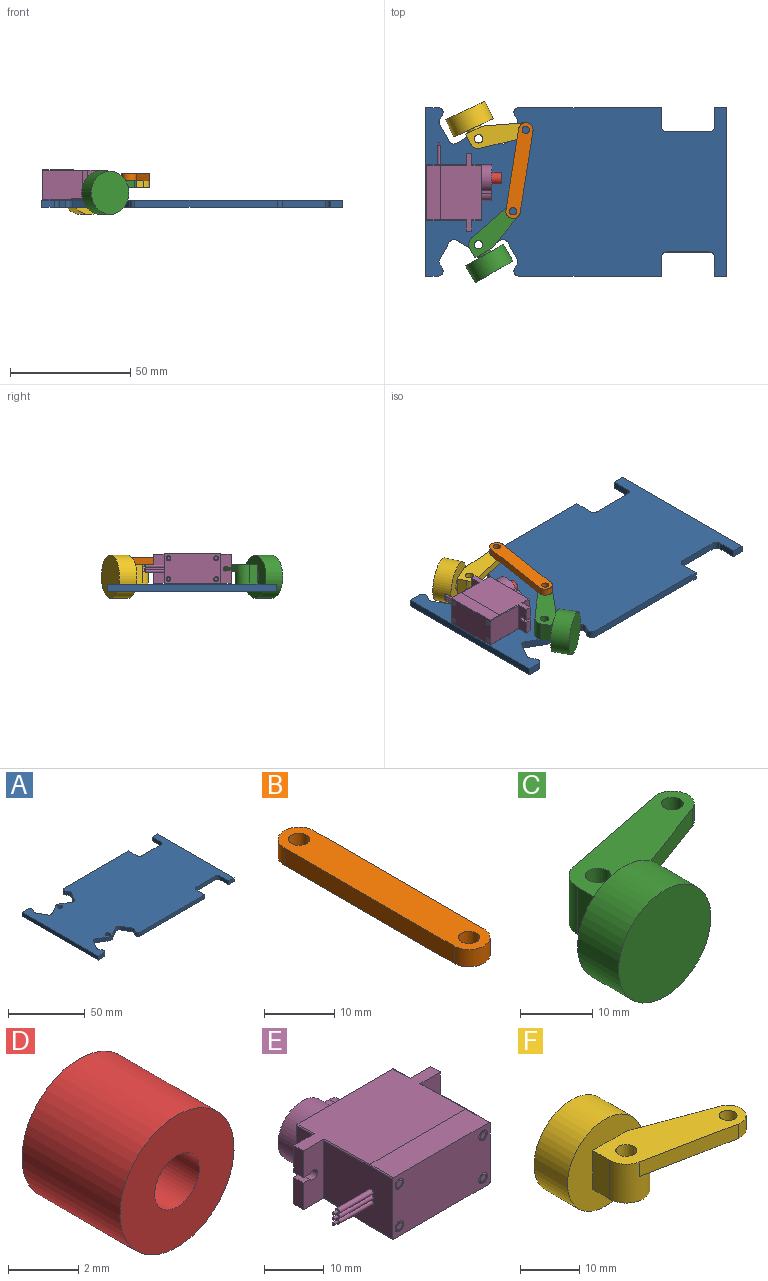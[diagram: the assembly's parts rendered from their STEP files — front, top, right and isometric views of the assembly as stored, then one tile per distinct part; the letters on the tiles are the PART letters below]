
ASSEMBLY  parts=6 mates=6
PART A: 48 faces, bbox 125x70x3 mm
  f0: plane 5.3x3mm, normal (0,-1,0), area 15.9mm2, adj f1,f45,f46,f47
  f1: cylinder r=2mm len=3.1mm, axis (0,0,-1), area 12.9mm2, adj f0,f2,f46,f47
  f2: cylinder r=18mm len=3mm, axis (0,0,-1), area 7.2mm2, adj f1,f3,f46,f47
  f3: cylinder r=2mm len=3mm, axis (0,0,-1), area 5.8mm2, adj f2,f4,f46,f47
  f4: plane 7.13x4.11mm, normal (0.87,-0.5,0), area 24.7mm2, adj f3,f5,f46,f47
  f5: cylinder r=2mm len=3mm, axis (0,0,-1), area 9.4mm2, adj f4,f6,f46,f47
  f6: plane 7.79x4.5mm, normal (-0.5,-0.87,0), area 27mm2, adj f5,f7,f46,f47
  f7: cylinder r=3mm len=3mm, axis (0,0,-1), area 9.4mm2, adj f6,f8,f46,f47
  f8: plane 7.79x4.5mm, normal (0.5,-0.87,0), area 27mm2, adj f7,f9,f46,f47
  f9: cylinder r=2mm len=3mm, axis (0,0,-1), area 9.4mm2, adj f8,f10,f46,f47
  f10: plane 7.13x4.11mm, normal (-0.87,-0.5,0), area 24.7mm2, adj f9,f11,f46,f47
  f11: cylinder r=2mm len=3mm, axis (0,0,-1), area 5.8mm2, adj f10,f12,f46,f47
  f12: cylinder r=18mm len=3mm, axis (0,0,-1), area 7.2mm2, adj f11,f13,f46,f47
  f13: cylinder r=2mm len=3.1mm, axis (0,0,-1), area 12.9mm2, adj f12,f14,f46,f47
  f14: plane 59.3x3mm, normal (0,-1,0), area 177.9mm2, adj f13,f15,f46,f47
  f15: plane 8x3mm, normal (1,0,0), area 24mm2, adj f14,f16,f46,f47
  f16: cylinder r=2mm len=3mm, axis (0,0,-1), area 9.4mm2, adj f15,f17,f46,f47
  f17: plane 18x3mm, normal (0,-1,0), area 54mm2, adj f16,f18,f46,f47
  f18: cylinder r=2mm len=3mm, axis (0,0,-1), area 9.4mm2, adj f17,f19,f46,f47
  f19: plane 8x3mm, normal (-1,0,0), area 24mm2, adj f18,f20,f46,f47
  f20: plane 5x3mm, normal (0,-1,0), area 15mm2, adj f19,f21,f46,f47
  f21: plane 70x3mm, normal (1,0,0), area 210mm2, adj f20,f22,f46,f47
  f22: plane 5x3mm, normal (0,1,0), area 15mm2, adj f21,f23,f46,f47
  f23: plane 8x3mm, normal (-1,0,0), area 24mm2, adj f22,f24,f46,f47
  f24: cylinder r=2mm len=3mm, axis (0,0,-1), area 9.4mm2, adj f23,f25,f46,f47
  f25: plane 18x3mm, normal (0,1,0), area 54mm2, adj f24,f26,f46,f47
  f26: cylinder r=2mm len=3mm, axis (0,0,-1), area 9.4mm2, adj f25,f27,f46,f47
  f27: plane 8x3mm, normal (1,0,0), area 24mm2, adj f26,f28,f46,f47
  f28: plane 59.3x3mm, normal (0,1,0), area 177.9mm2, adj f27,f29,f46,f47
  f29: cylinder r=2mm len=3.1mm, axis (0,0,-1), area 12.9mm2, adj f28,f30,f46,f47
  f30: cylinder r=18mm len=3mm, axis (0,0,-1), area 7.2mm2, adj f29,f31,f46,f47
  f31: cylinder r=2mm len=3mm, axis (0,0,-1), area 5.8mm2, adj f30,f32,f46,f47
  f32: plane 7.13x4.11mm, normal (-0.87,0.5,0), area 24.7mm2, adj f31,f33,f46,f47
  f33: cylinder r=2mm len=3mm, axis (0,0,-1), area 9.4mm2, adj f32,f34,f46,f47
  f34: plane 7.79x4.5mm, normal (0.5,0.87,0), area 27mm2, adj f33,f35,f46,f47
  f35: cylinder r=3mm len=3mm, axis (0,0,-1), area 9.4mm2, adj f34,f36,f46,f47
  f36: plane 7.79x4.5mm, normal (-0.5,0.87,0), area 27mm2, adj f35,f37,f46,f47
  f37: cylinder r=2mm len=3mm, axis (0,0,-1), area 9.4mm2, adj f36,f38,f46,f47
  f38: plane 7.13x4.11mm, normal (0.87,0.5,0), area 24.7mm2, adj f37,f39,f46,f47
  f39: cylinder r=2mm len=3mm, axis (0,0,-1), area 5.8mm2, adj f38,f40,f46,f47
  f40: cylinder r=18mm len=3mm, axis (0,0,-1), area 7.2mm2, adj f39,f41,f46,f47
  f41: cylinder r=2mm len=3.1mm, axis (0,0,-1), area 12.9mm2, adj f40,f42,f46,f47
  f42: plane 5.3x3mm, normal (0,1,0), area 15.9mm2, adj f41,f45,f46,f47
  f43: cylinder r=1.75mm len=3.5mm, axis (0,0,-1), area 33mm2, adj f46,f47
  f44: cylinder r=1.75mm len=3.5mm, axis (0,0,-1), area 33mm2, adj f46,f47
  f45: plane 70x3mm, normal (-1,0,0), area 210mm2, adj f0,f42,f46,f47
  f46: plane 125x70mm, normal (0,0,1), area 7517.5mm2, adj f0,f1,f2,f3,f4,f5,f6,f7
  f47: plane 125x70mm, normal (0,0,-1), area 7517.5mm2, adj f0,f1,f2,f3,f4,f5,f6,f7
PART B: 8 faces, bbox 6x40.2x3 mm
  f0: plane 34.19x3mm, normal (-1,0,0), area 102.6mm2, adj f1,f4,f6,f7
  f1: cylinder r=3mm len=6mm, axis (0,0,-1), area 28.3mm2, adj f0,f2,f6,f7
  f2: plane 34.19x3mm, normal (1,0,0), area 102.6mm2, adj f1,f4,f6,f7
  f3: cylinder r=1.5mm len=3mm, axis (0,0,-1), area 28.3mm2, adj f6,f7
  f4: cylinder r=3mm len=6mm, axis (0,0,-1), area 28.3mm2, adj f0,f2,f6,f7
  f5: cylinder r=1.5mm len=3mm, axis (0,0,-1), area 28.3mm2, adj f6,f7
  f6: plane 40.19x6mm, normal (0,0,1), area 219.3mm2, adj f0,f1,f2,f3,f4,f5
  f7: plane 40.19x6mm, normal (0,0,-1), area 219.3mm2, adj f0,f1,f2,f3,f4,f5
PART C: 16 faces, bbox 31.4x20.9x18 mm
  f0: plane 5x4mm, normal (1,0,0), area 20mm2, adj f1,f4,f6,f15
  f1: cylinder r=4mm len=8mm, axis (0,0,-1), area 79.3mm2, adj f0,f2,f5,f6,f13,f15
  f2: plane 8x4mm, normal (-1,0,0), area 32mm2, adj f1,f4,f5,f6
  f3: cylinder r=1.75mm len=8mm, axis (0,0,-1), area 88mm2, adj f5,f6
  f4: plane 8x8mm, normal (0,-1,0), area 35.7mm2, adj f0,f2,f5,f6,f7,f11
  f5: plane 26.39x11.9mm, normal (0,0,1), area 176.5mm2, adj f1,f2,f3,f4,f11,f12,f13,f14
  f6: plane 8x8mm, normal (0,0,-1), area 47.5mm2, adj f0,f1,f2,f3,f4
  f7: cylinder r=3mm len=6mm, axis (0,1,0), area 18.8mm2, adj f4,f10
  f8: cylinder r=9mm len=18mm, axis (0,1,0), area 452.4mm2, adj f9,f10
  f9: plane 18x18mm, normal (0,-1,0), area 254.5mm2, adj f8
  f10: plane 18x18mm, normal (0,1,0), area 226.2mm2, adj f7,f8
  f11: plane 16.43x6.09mm, normal (0.35,-0.94,0), area 52.6mm2, adj f4,f5,f12,f15
  f12: cylinder r=3mm len=5.81mm, axis (0,0,1), area 26.9mm2, adj f5,f11,f13,f15
  f13: plane 19.59x3.92mm, normal (-0.2,0.98,0), area 59.9mm2, adj f1,f5,f12,f15
  f14: cylinder r=1.5mm len=3mm, axis (0,0,1), area 28.3mm2, adj f5,f15
  f15: plane 23.18x11.9mm, normal (0,0,-1), area 129mm2, adj f0,f1,f11,f12,f13,f14
PART D: 4 faces, bbox 4.6x4x4.6 mm
  f0: cylinder r=2.3mm len=4.6mm, axis (0,1,0), area 57.1mm2, adj f1,f3
  f1: plane 4.6x4.6mm, normal (0,-1,0), area 14.1mm2, adj f0,f2
  f2: cylinder r=0.9mm len=3.95mm, axis (0,1,0), area 22.3mm2, adj f1,f3
  f3: plane 4.6x4.6mm, normal (0,1,0), area 14.1mm2, adj f0,f2
PART E: 75 faces, bbox 36.7x27x12.6 mm
  f0: plane 1x1mm, normal (-1,0,0), area 0.6mm2, adj f50,f55
  f1: plane 1x1mm, normal (-1,0,0), area 0.6mm2, adj f49,f53
  f2: plane 1x1mm, normal (-1,0,0), area 0.6mm2, adj f48,f51
  f3: plane 16.34x12.19mm, normal (-1,0,0), area 193.9mm2, adj f9,f17,f48,f49,f50,f61,f62,f63
  f4: plane 12.04x4.84mm, normal (0,-1,0), area 51.4mm2, adj f5,f13,f14,f24,f25,f29,f30,f31
  f5: plane 5.48x2.32mm, normal (1,0,0), area 12.6mm2, adj f4,f6,f25,f30
  f6: plane 11.93x4.84mm, normal (0,1,0), area 50.8mm2, adj f5,f14,f15,f24,f25,f29,f30,f31
  f7: plane 11.93x4.84mm, normal (0,1,0), area 50.8mm2, adj f8,f11,f12,f24,f25,f26,f27,f28
  f8: plane 5.48x2.32mm, normal (-1,0,0), area 12.6mm2, adj f7,f9,f24,f27
  f9: plane 12.04x4.84mm, normal (0,-1,0), area 51.4mm2, adj f3,f8,f12,f24,f25,f26,f27,f28
  f10: plane 23.03x11.72mm, normal (0,1,0), area 149mm2, adj f11,f15,f19,f20,f21,f22,f24,f25
  f11: plane 11.53x4.06mm, normal (-1,0,0), area 46.4mm2, adj f7,f10,f71,f72
  f12: plane 5.48x2.32mm, normal (-1,0,0), area 12.6mm2, adj f7,f9,f25,f28
  f13: plane 16.34x12.19mm, normal (1,0,0), area 196.2mm2, adj f4,f17,f65,f66,f67,f68
  f14: plane 5.48x2.32mm, normal (1,0,0), area 12.6mm2, adj f4,f6,f24,f31
  f15: plane 11.53x4.06mm, normal (1,0,0), area 46.4mm2, adj f6,f10,f69,f70
  f16: plane 22.63x5.5mm, normal (0,0,1), area 124.5mm2, adj f17,f25,f61,f65
  f17: plane 23.03x12.59mm, normal (0,-1,0), area 277.3mm2, adj f3,f13,f16,f18,f32,f36,f40,f44
  f18: plane 22.63x5.5mm, normal (0,0,-1), area 124.5mm2, adj f17,f24,f63,f67
  f19: cylinder r=5.72mm len=11.45mm, axis (0,-1,0), area 128.4mm2, adj f10,f20,f22,f23
  f20: plane 4.28x1.41mm, normal (0,0,1), area 6mm2, adj f10,f19,f21,f23
  f21: cylinder r=2.85mm len=5.7mm, axis (0,-1,0), area 38.3mm2, adj f10,f20,f22,f23
  f22: plane 4.28x1.41mm, normal (0,0,-1), area 6mm2, adj f10,f19,f21,f23
  f23: plane 14.95x11.45mm, normal (0,1,0), area 103.5mm2, adj f19,f20,f21,f22,f73
  f24: plane 32.31x17.22mm, normal (0,0.03,-1), area 412.3mm2, adj f4,f6,f7,f8,f9,f10,f14,f18
  f25: plane 32.31x17.22mm, normal (0,0.03,1), area 412.3mm2, adj f4,f5,f6,f7,f9,f10,f12,f16
  f26: cylinder r=0.97mm len=2.32mm, axis (0,-1,0), area 11.5mm2, adj f7,f9,f27,f28
  f27: plane 2.32x1.51mm, normal (0,0,1), area 3.5mm2, adj f7,f8,f9,f26
  f28: plane 2.32x1.51mm, normal (0,0,-1), area 3.5mm2, adj f7,f9,f12,f26
  f29: cylinder r=0.97mm len=2.32mm, axis (0,-1,0), area 11.5mm2, adj f4,f6,f30,f31
  f30: plane 2.32x1.51mm, normal (0,0,-1), area 3.5mm2, adj f4,f5,f6,f29
  f31: plane 2.32x1.51mm, normal (0,0,1), area 3.5mm2, adj f4,f6,f14,f29
  f32: cylinder r=1mm len=2mm, axis (0,-1,0), area 6.3mm2, adj f17,f33
  f33: plane 2x2mm, normal (0,-1,0), area 0.2mm2, adj f32,f34
  f34: cylinder r=0.97mm len=1.95mm, axis (0,-1,0), area 4.3mm2, adj f33,f60
  f35: plane 1.35x1.35mm, normal (0,-1,0), area 1.4mm2, adj f60
  f36: cylinder r=1mm len=2mm, axis (0,-1,0), area 6.3mm2, adj f17,f37
  f37: plane 2x2mm, normal (0,-1,0), area 0.2mm2, adj f36,f38
  f38: cylinder r=0.97mm len=1.95mm, axis (0,-1,0), area 4.3mm2, adj f37,f59
  f39: plane 1.35x1.35mm, normal (0,-1,0), area 1.4mm2, adj f59
  f40: cylinder r=1mm len=2mm, axis (0,-1,0), area 6.3mm2, adj f17,f41
  f41: plane 2x2mm, normal (0,-1,0), area 0.2mm2, adj f40,f42
  f42: cylinder r=0.97mm len=1.95mm, axis (0,-1,0), area 4.3mm2, adj f41,f57
  f43: plane 1.35x1.35mm, normal (0,-1,0), area 1.4mm2, adj f57
  f44: cylinder r=1mm len=2mm, axis (0,-1,0), area 6.3mm2, adj f17,f45
  f45: plane 2x2mm, normal (0,-1,0), area 0.2mm2, adj f44,f46
  f46: cylinder r=0.97mm len=1.95mm, axis (0,-1,0), area 4.3mm2, adj f45,f58
  f47: plane 1.35x1.35mm, normal (0,-1,0), area 1.4mm2, adj f58
  f48: cylinder r=0.5mm len=8mm, axis (1,0,0), area 25.1mm2, adj f2,f3
  f49: cylinder r=0.5mm len=8mm, axis (1,0,0), area 25.1mm2, adj f1,f3
  f50: cylinder r=0.5mm len=8mm, axis (1,0,0), area 25.1mm2, adj f0,f3
  f51: cylinder r=0.25mm len=1mm, axis (1,0,0), area 1.6mm2, adj f2,f52
  f52: plane 0.5x0.5mm, normal (-1,0,0), area 0.2mm2, adj f51
  f53: cylinder r=0.25mm len=1mm, axis (1,0,0), area 1.6mm2, adj f1,f54
  f54: plane 0.5x0.5mm, normal (-1,0,0), area 0.2mm2, adj f53
  f55: cylinder r=0.25mm len=1mm, axis (1,0,0), area 1.6mm2, adj f0,f56
  f56: plane 0.5x0.5mm, normal (-1,0,0), area 0.2mm2, adj f55
  f57: torus R=0.68mm, axis (0,1,0), area 2.6mm2, adj f42,f43
  f58: torus R=0.68mm, axis (0,1,0), area 2.6mm2, adj f46,f47
  f59: torus R=0.68mm, axis (0,1,0), area 2.6mm2, adj f38,f39
  f60: torus R=0.68mm, axis (0,1,0), area 2.6mm2, adj f34,f35
  f61: cylinder r=0.2mm len=5.5mm, axis (0,1,0), area 1.7mm2, adj f3,f16,f17,f62
  f62: cylinder r=0.2mm len=10.85mm, axis (0,1,-0.03), area 3.4mm2, adj f3,f9,f25,f61
  f63: cylinder r=0.2mm len=5.5mm, axis (0,-1,0), area 1.7mm2, adj f3,f17,f18,f64
  f64: cylinder r=0.2mm len=10.85mm, axis (0,-1,-0.03), area 3.4mm2, adj f3,f9,f24,f63
  f65: cylinder r=0.2mm len=5.5mm, axis (0,-1,0), area 1.7mm2, adj f13,f16,f17,f66
  f66: cylinder r=0.2mm len=10.85mm, axis (0,-1,0.03), area 3.4mm2, adj f4,f13,f25,f65
  f67: cylinder r=0.2mm len=5.5mm, axis (0,1,0), area 1.7mm2, adj f13,f17,f18,f68
  f68: cylinder r=0.2mm len=10.85mm, axis (0,1,0.03), area 3.4mm2, adj f4,f13,f24,f67
  f69: cylinder r=0.2mm len=4.07mm, axis (0,1,0.03), area 1.3mm2, adj f6,f10,f15,f24
  f70: cylinder r=0.2mm len=4.07mm, axis (0,-1,0.03), area 1.3mm2, adj f6,f10,f15,f25
  f71: cylinder r=0.2mm len=4.07mm, axis (0,-1,-0.03), area 1.3mm2, adj f7,f10,f11,f24
  f72: cylinder r=0.2mm len=4.07mm, axis (0,1,-0.03), area 1.3mm2, adj f7,f10,f11,f25
  f73: cylinder r=2.35mm len=4.7mm, axis (0,1,0), area 30.3mm2, adj f23,f74
  f74: plane 4.7x4.7mm, normal (0,1,0), area 17.3mm2, adj f73
PART F: 16 faces, bbox 31.4x20.9x18 mm
  f0: plane 5x4mm, normal (1,0,0), area 20mm2, adj f1,f4,f6,f15
  f1: cylinder r=4mm len=8mm, axis (0,0,-1), area 79.3mm2, adj f0,f2,f5,f6,f13,f15
  f2: plane 8x4mm, normal (-1,0,0), area 32mm2, adj f1,f4,f5,f6
  f3: cylinder r=1.75mm len=8mm, axis (0,0,-1), area 88mm2, adj f5,f6
  f4: plane 8x8mm, normal (0,1,0), area 35.7mm2, adj f0,f2,f5,f6,f7,f11
  f5: plane 26.39x11.9mm, normal (0,0,1), area 176.5mm2, adj f1,f2,f3,f4,f11,f12,f13,f14
  f6: plane 8x8mm, normal (0,0,-1), area 47.5mm2, adj f0,f1,f2,f3,f4
  f7: cylinder r=3mm len=6mm, axis (0,-1,0), area 18.8mm2, adj f4,f10
  f8: cylinder r=9mm len=18mm, axis (0,-1,0), area 452.4mm2, adj f9,f10
  f9: plane 18x18mm, normal (0,1,0), area 254.5mm2, adj f8
  f10: plane 18x18mm, normal (0,-1,0), area 226.2mm2, adj f7,f8
  f11: plane 16.43x6.09mm, normal (0.35,0.94,0), area 52.6mm2, adj f4,f5,f12,f15
  f12: cylinder r=3mm len=5.81mm, axis (0,0,1), area 26.9mm2, adj f5,f11,f13,f15
  f13: plane 19.59x3.92mm, normal (-0.2,-0.98,0), area 59.9mm2, adj f1,f5,f12,f15
  f14: cylinder r=1.5mm len=3mm, axis (0,0,1), area 28.3mm2, adj f5,f15
  f15: plane 23.18x11.9mm, normal (0,0,-1), area 129mm2, adj f0,f1,f11,f12,f13,f14
PLACE A t=(20.08,-2.87,-27.82)mm fixed
PLACE B rot(axis=(0,0,-1),8.9deg) t=(17.44,2.68,-28.32)mm
PLACE C rot(axis=(0,0,1),29.9deg) t=(3.71,14.4,-28.32)mm
PLACE D rot(axis=(0.64,-0.64,0.43),133.7deg) t=(-1.24,2.17,-17.16)mm
PLACE E rot(axis=(0,0,-1),90deg) t=(-25.51,1.3,-18.46)mm
PLACE F rot(axis=(0,0,1),24.9deg) t=(25.58,16.2,-28.32)mm
MATE revolute D.f0 <-> E.f19  axis (-1,0,0) through (-14.85,2.7,-18.46)mm
MATE revolute B.f3 <-> F.f12  axis (0,0,-1) through (-0.76,22.84,-16.82)mm
MATE revolute F.f1 <-> A.f30  axis (0,0,-1) through (-20.42,19.13,-24.82)mm
MATE parallel E.f17 <-> A.f45  axis (-1,0,0) through (-41.85,-3.09,-24.75)mm
MATE revolute C.f1 <-> A.f2  axis (0,0,-1) through (-20.42,-24.87,-24.82)mm
MATE revolute B.f1 <-> C.f12  axis (0,0,-1) through (-6.06,-10.95,-16.82)mm
